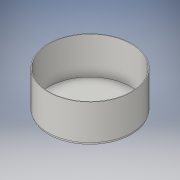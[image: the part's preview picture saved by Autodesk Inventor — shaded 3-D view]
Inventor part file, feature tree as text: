
AUTODESK INVENTOR PART (.ipt)
format: ipt  version: 2016 SP1 (Build 200210100, 210)  size: 123,904 bytes
history: native  units: in
note: dims shown in document units (in); Inventor stores cm internally (conversion verified against a paired STEP export)
features: extrude x2, sketch x2, fillet x1
ambient origin geometry x8: Origin, YZ Plane, XZ Plane, XY Plane, X Axis, Y Axis, Z Axis, Center Point
bodies: Solid1 (feature_tree)
feature tree (5):
  extrude  "Extrusion1"  Depth=6.0in TaperAngle=0.0deg
  extrude  "Extrusion2"  Depth=5.8in TaperAngle=0.0deg
  fillet  "Fillet1"  Radius=0.5in
  sketch  "Sketch1"  dims[d0=13.1in d1=6.0in d2=0.0in]
  sketch  "Sketch2"  dims[d3=12.9in d4=5.8in d5=0.0in d6=0.5in]
